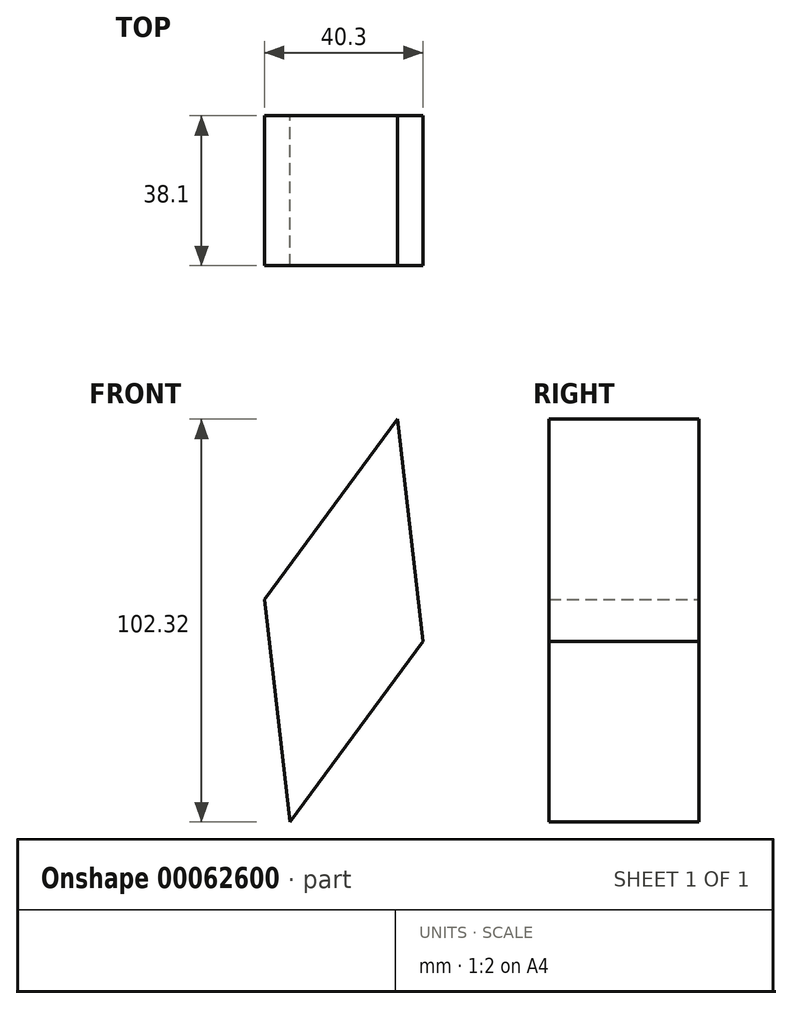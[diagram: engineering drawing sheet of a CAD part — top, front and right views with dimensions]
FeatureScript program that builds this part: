
annotation { "Feature Type Name" : "Feature", "Feature Type Description" : "" }
export const myFeature = defineFeature(function(context is Context, id is Id, definition is map)
    precondition{}
    {
        {
            var Q0;
            Q0=qCreatedBy(makeId("Front.planeOp"),FACE);
            var sketch = newSketch(context, id + "F0", { "sketchPlane" : qUnion([Q0])});
            skLineSegment(sketch, "E0", {"start": v(0, 0) * mm, "end": v(6.54, -56.52) * mm});
            skLineSegment(sketch, "E1", {"start": v(6.54, -56.52) * mm, "end": v(40.3, -10.72) * mm});
            skLineSegment(sketch, "E2", {"start": v(40.3, -10.72) * mm, "end": v(33.76, 45.8) * mm});
            skLineSegment(sketch, "E3", {"start": v(33.76, 45.8) * mm, "end": v(0, 0) * mm});
            skSolve(sketch);
        }
        {
            var Q0;
            Q0=makeQuery(id+"F0.imprint","IMPRINT",FACE,{"disambiguationData":[TD([[makeQuery(id+"F0.imprint","IMPRINT",EDGE,{"derivedFrom":sQuery(id+"F0.wireOp",EDGE,"E0")}),1.0]])]});
            extrude(context, id + "F1", {"entities" : qUnion([Q0]), "depth" : 38.1 * mm});
        }
    });
